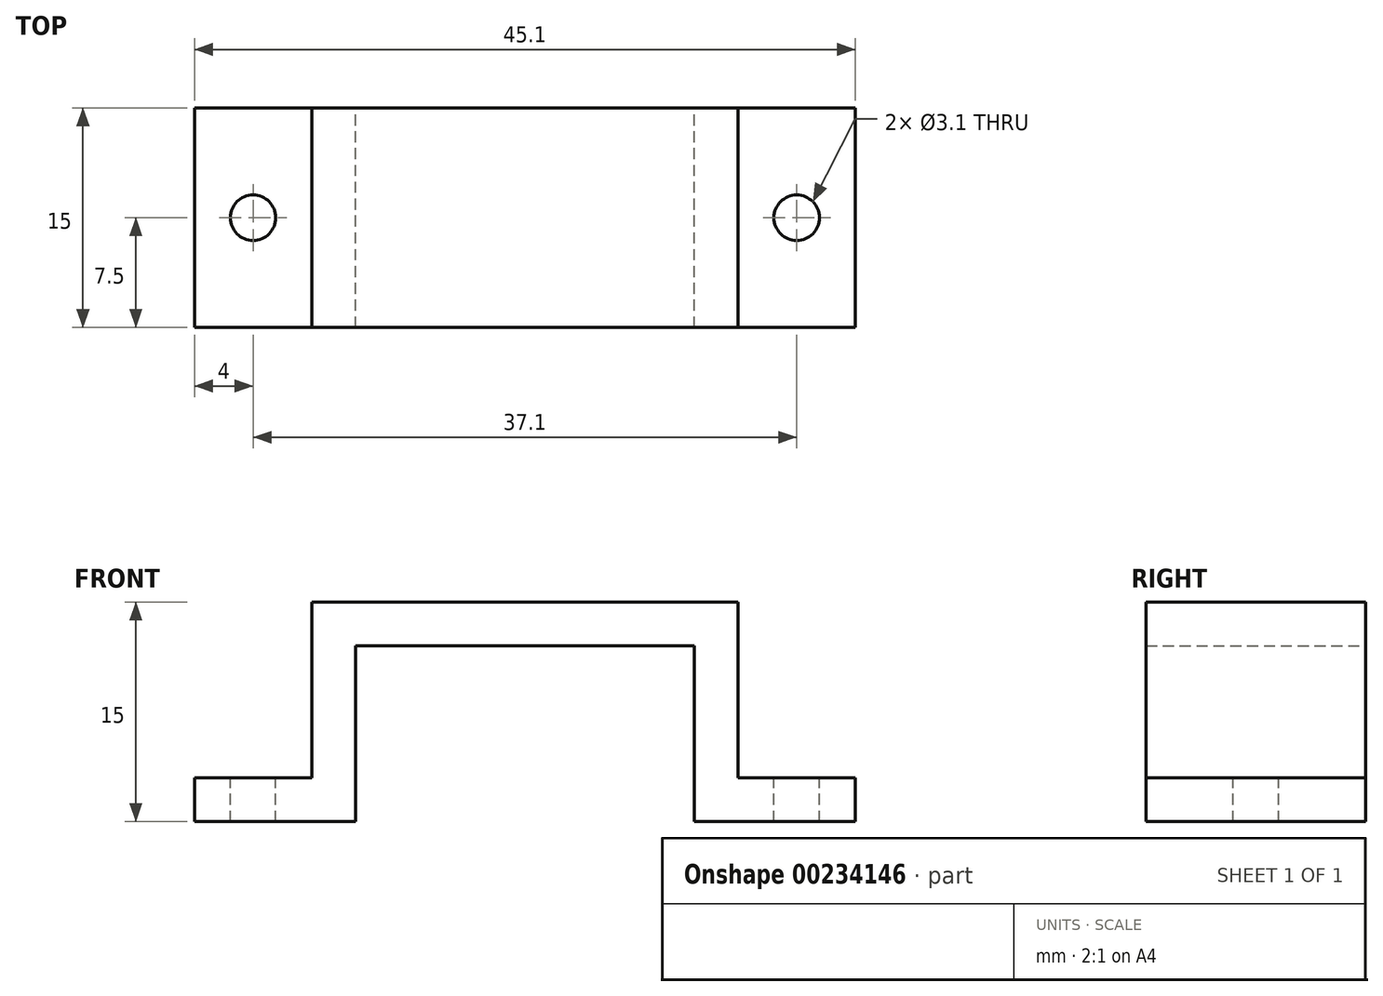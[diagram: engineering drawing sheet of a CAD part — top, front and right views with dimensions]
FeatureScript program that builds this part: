
annotation { "Feature Type Name" : "Feature", "Feature Type Description" : "" }
export const myFeature = defineFeature(function(context is Context, id is Id, definition is map)
    precondition{}
    {
        {
            var Q0;
            Q0=qCreatedBy(makeId("Front.planeOp"),FACE);
            var sketch = newSketch(context, id + "F0", { "sketchPlane" : qUnion([Q0])});
            skLineSegment(sketch, "E0.bottom", {"start": v(0, 12) * mm, "end": v(-11.55, 12) * mm});
            skLineSegment(sketch, "E0.top", {"start": v(0, 15) * mm, "end": v(-14.55, 15) * mm});
            skLineSegment(sketch, "E0.right", {"start": v(-14.55, 12) * mm, "end": v(-14.55, 15) * mm});
            skLineSegment(sketch, "E1.bottom", {"start": v(-11.55, 15) * mm, "end": v(-14.55, 15) * mm});
            skLineSegment(sketch, "E1.top", {"start": v(-11.55, 0) * mm, "end": v(-14.55, 0) * mm});
            skLineSegment(sketch, "E1.left", {"start": v(-11.55, 12) * mm, "end": v(-11.55, 0) * mm});
            skLineSegment(sketch, "E1.right", {"start": v(-14.55, 15) * mm, "end": v(-14.55, 3) * mm});
            skLineSegment(sketch, "E2.bottom", {"start": v(-14.55, 3) * mm, "end": v(-22.55, 3) * mm});
            skLineSegment(sketch, "E2.top", {"start": v(-11.55, 0) * mm, "end": v(-22.55, 0) * mm});
            skLineSegment(sketch, "E2.left", {"start": v(-11.55, 3) * mm, "end": v(-11.55, 0) * mm});
            skLineSegment(sketch, "E2.right", {"start": v(-22.55, 3) * mm, "end": v(-22.55, 0) * mm});
            skLineSegment(sketch, "E3.MirrorCS", {"start": v(0, 15) * mm, "end": v(14.55, 15) * mm});
            skLineSegment(sketch, "E4.MirrorCS", {"start": v(0, 12) * mm, "end": v(11.55, 12) * mm});
            skLineSegment(sketch, "E5.MirrorCS", {"start": v(11.55, 12) * mm, "end": v(11.55, 0) * mm});
            skLineSegment(sketch, "E6.MirrorCS", {"start": v(14.55, 15) * mm, "end": v(14.55, 3) * mm});
            skLineSegment(sketch, "E7.MirrorCS", {"start": v(14.55, 3) * mm, "end": v(22.55, 3) * mm});
            skLineSegment(sketch, "E8.MirrorCS", {"start": v(11.55, 0) * mm, "end": v(22.55, 0) * mm});
            skLineSegment(sketch, "E9.MirrorCS", {"start": v(22.55, 3) * mm, "end": v(22.55, 0) * mm});
            skSolve(sketch);
        }
        {
            var Q0;
            Q0=makeQuery(id+"F0.imprint","IMPRINT",FACE,{"disambiguationData":[TD([[makeQuery(id+"F0.imprint","IMPRINT",EDGE,{"derivedFrom":sQuery(id+"F0.wireOp",EDGE,"E0.bottom")}),-1.0]])]});
            extrude(context, id + "F1", {"entities" : qUnion([Q0]), "depth" : 15 * mm});
        }
        {
            var Q0;
            Q0=makeQuery(id+"F1.opExtrude","SWEPT_FACE",FACE,{"disambiguationData":[OSD([sQuery(id+"F0.wireOp",EDGE,"E7.MirrorCS")])]});
            var sketch = newSketch(context, id + "F2", { "sketchPlane" : qUnion([Q0])});
            skCircle(sketch, "E10", {"center": v(18.55, -7.5) * mm, "radius": 1.55 * mm});
            skCircle(sketch, "E11", {"center": v(-18.55, -7.5) * mm, "radius": 1.55 * mm});
            skSolve(sketch);
        }
        {
            var Q0;
            Q0=makeQuery(id+"F2.imprint","IMPRINT",FACE,{"disambiguationData":[TD([[makeQuery(id+"F2.imprint","IMPRINT",EDGE,{"derivedFrom":sQuery(id+"F2.wireOp",EDGE,"E11")}),1.0]])]});
            var Q1;
            Q1=makeQuery(id+"F2.imprint","IMPRINT",FACE,{"disambiguationData":[TD([[makeQuery(id+"F2.imprint","IMPRINT",EDGE,{"derivedFrom":sQuery(id+"F2.wireOp",EDGE,"E10")}),1.0]])]});
            extrude(context, id + "F3", {"entities" : qUnion([Q0, Q1]), "operationType" : NewBodyOperationType.REMOVE, "endBound" : BoundingType.THROUGH_ALL, "oppositeDirection" : true, "depth" : 25 * mm});
        }
    });
